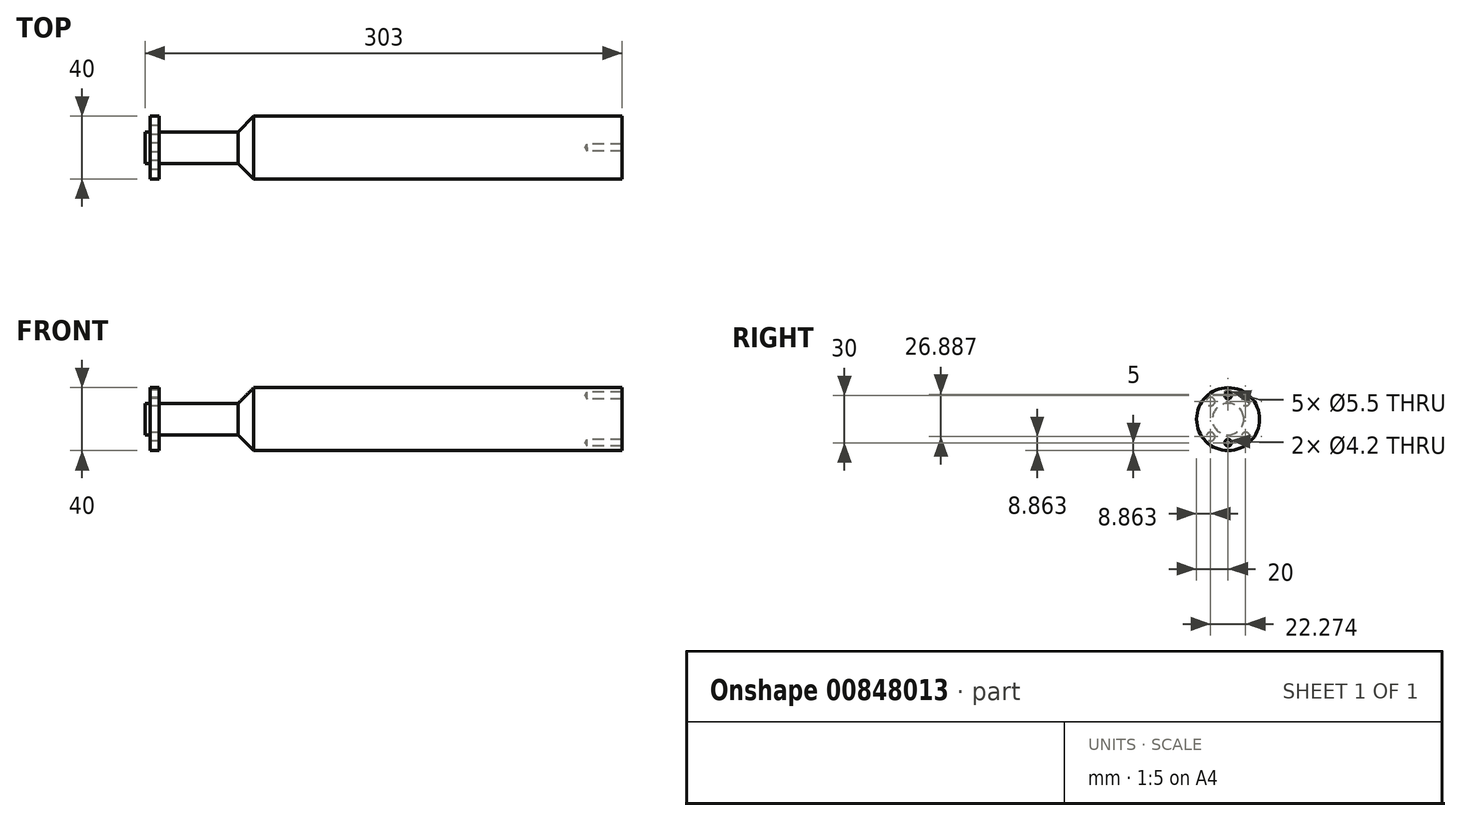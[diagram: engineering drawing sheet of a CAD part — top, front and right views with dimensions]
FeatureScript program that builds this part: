
annotation { "Feature Type Name" : "Feature", "Feature Type Description" : "" }
export const myFeature = defineFeature(function(context is Context, id is Id, definition is map)
    precondition{}
    {
        {
            var Q0;
            Q0=qCreatedBy(makeId("Front.planeOp"),FACE);
            var sketch = newSketch(context, id + "F0", { "sketchPlane" : qUnion([Q0])});
            skLineSegment(sketch, "E0", {"start": v(-163.2, 0) * mm, "end": v(136.8, 0) * mm});
            skLineSegment(sketch, "E1", {"start": v(136.8, 0) * mm, "end": v(136.8, 20) * mm});
            skLineSegment(sketch, "E2", {"start": v(136.8, 20) * mm, "end": v(-97.2, 20) * mm});
            skLineSegment(sketch, "E3", {"start": v(-97.2, 20) * mm, "end": v(-107.2, 10) * mm});
            skLineSegment(sketch, "E4", {"start": v(-107.2, 10) * mm, "end": v(-156.7, 10) * mm});
            skLineSegment(sketch, "E5", {"start": v(-157.2, 10.5) * mm, "end": v(-157.2, 20) * mm});
            skLineSegment(sketch, "E6", {"start": v(-163.2, 20) * mm, "end": v(-163.2, 10.5) * mm});
            skLineSegment(sketch, "E7", {"start": v(-163.7, 10) * mm, "end": v(-166.2, 10) * mm});
            skLineSegment(sketch, "E8", {"start": v(-166.2, 10) * mm, "end": v(-166.2, 0) * mm});
            skLineSegment(sketch, "E9", {"start": v(-166.2, 0) * mm, "end": v(-163.2, 0) * mm});
            skLineSegment(sketch, "E10", {"start": v(-163.2, 20) * mm, "end": v(-157.2, 20) * mm});
            skPoint(sketch, "E11.visualSharp", {"position": v(-157.2, 10) * mm});
            skArc(sketch, "E11.filletArc", {"start": v(-157.2, 10.5) * mm, "mid": v(-157.05, 10.15) * mm, "end": v(-156.7, 10) * mm});
            skPoint(sketch, "E12.visualSharp", {"position": v(-163.2, 10) * mm});
            skArc(sketch, "E12.filletArc", {"start": v(-163.7, 10) * mm, "mid": v(-163.34, 10.15) * mm, "end": v(-163.2, 10.5) * mm});
            skLineSegment(sketch, "E13", {"start": v(-204.84, 0) * mm, "end": v(203.32, 0) * mm, "construction": true});
            skSolve(sketch);
        }
        {
            var Q0;
            Q0=makeQuery(id+"F0.imprint","IMPRINT",FACE,{"disambiguationData":[TD([[makeQuery(id+"F0.imprint","IMPRINT",EDGE,{"derivedFrom":sQuery(id+"F0.wireOp",EDGE,"E0")}),1.0]])]});
            var Q1;
            Q1 = qConstructionFilter(qBodyType(qCreatedBy(id + "F0" ,EDGE), BodyType.WIRE), ConstructionObject.NO);
            var Q2;
            Q2=sQuery(id+"F0.wireOp",EDGE,"E13");
            revolve(context, id + "F1", {"surfaceOperationType" : NewSurfaceOperationType.NEW, "entities" : qUnion([Q0]), "surfaceEntities" : qUnion([Q1]), "axis" : qUnion([Q2]), "revolveType" : RevolveType.FULL});
        }
        {
            var Q0;
            Q0=makeQuery(id+"F1.opRevolve","SWEPT_FACE",FACE,{"disambiguationData":[OSD([sQuery(id+"F0.wireOp",EDGE,"E6")])]});
            var sketch = newSketch(context, id + "F2", { "sketchPlane" : qUnion([Q0])});
            skLineSegment(sketch, "E14", {"start": v(0, 0) * mm, "end": v(0, 29.49) * mm, "construction": true});
            skCircle(sketch, "E15", {"center": v(0, 0) * mm, "radius": 15.75 * mm, "construction": true});
            skCircle(sketch, "E16", {"center": v(0, 15.75) * mm, "radius": 2.75 * mm});
            skLineSegment(sketch, "E17", {"start": v(0, 0) * mm, "end": v(-11.14, 11.14) * mm, "construction": true});
            skCircle(sketch, "E18", {"center": v(-11.14, 11.14) * mm, "radius": 2.75 * mm});
            skCircle(sketch, "E19.1.0", {"center": v(-11.14, -11.14) * mm, "radius": 2.75 * mm});
            skCircle(sketch, "E19.2.0", {"center": v(11.14, -11.14) * mm, "radius": 2.75 * mm});
            skCircle(sketch, "E19.3.0", {"center": v(11.14, 11.14) * mm, "radius": 2.75 * mm});
            skLineSegment(sketch, "E20", {"start": v(0, 0) * mm, "end": v(-11.14, -11.14) * mm, "construction": true});
            skLineSegment(sketch, "E21", {"start": v(0, 0) * mm, "end": v(11.14, -11.14) * mm, "construction": true});
            skLineSegment(sketch, "E22", {"start": v(0, 0) * mm, "end": v(11.14, 11.14) * mm, "construction": true});
            skSolve(sketch);
        }
        {
            var Q0;
            Q0 = qSketchRegion(id + "F2", true);
            extrude(context, id + "F3", {"entities" : qUnion([Q0]), "operationType" : NewBodyOperationType.REMOVE, "oppositeDirection" : true, "depth" : 25 * mm, "offsetDistance" : 25 * mm});
        }
        {
            var Q0;
            Q0=makeQuery(id+"F1.opRevolve","SWEPT_FACE",FACE,{"disambiguationData":[OSD([sQuery(id+"F0.wireOp",EDGE,"E1")])]});
            var sketch = newSketch(context, id + "F4", { "sketchPlane" : qUnion([Q0])});
            skLineSegment(sketch, "E23", {"start": v(0, -20) * mm, "end": v(0, 20) * mm, "construction": true});
            skLineSegment(sketch, "E24", {"start": v(-20, 0) * mm, "end": v(20, 0) * mm, "construction": true});
            skCircle(sketch, "E25", {"center": v(0, 0) * mm, "radius": 15 * mm, "construction": true});
            skPoint(sketch, "E26", {"position": v(0, 15) * mm});
            skPoint(sketch, "E27", {"position": v(0, -15) * mm});
            skSolve(sketch);
        }
        {
            var Q0;
            Q0=sQuery(id+"F4.wireOp",VERTEX,"E26");
            var Q1;
            Q1=sQuery(id+"F4.wireOp",VERTEX,"E27");
            var Q2;
            Q2=makeQuery(id+"F1.opRevolve","SWEPT_BODY",BODY,{"disambiguationData":[OSD([sQuery(id+"F0.wireOp",EDGE,"E0"),sQuery(id+"F0.wireOp",EDGE,"E1"),sQuery(id+"F0.wireOp",EDGE,"E2"),sQuery(id+"F0.wireOp",EDGE,"E3"),sQuery(id+"F0.wireOp",EDGE,"E4"),sQuery(id+"F0.wireOp",EDGE,"E5"),sQuery(id+"F0.wireOp",EDGE,"E6"),sQuery(id+"F0.wireOp",EDGE,"E7"),sQuery(id+"F0.wireOp",EDGE,"E8"),sQuery(id+"F0.wireOp",EDGE,"E9"),sQuery(id+"F0.wireOp",EDGE,"E10"),sQuery(id+"F0.wireOp",EDGE,"E11.filletArc"),sQuery(id+"F0.wireOp",EDGE,"E12.filletArc")])]});
            hole(context, id + "F5", {"style" : HoleStyle.SIMPLE, "endStyle" : HoleEndStyle.BLIND, "standardTappedOrClearance" : lookupTablePath({ "standard" : "ISO", "engagement" : "75%", "pitch" : "0.8 mm", "size" : "M5", "type" : "Tapped" }), "standardBlindInLast" : lookupTablePath({ "standard" : "ISO", "engagement" : "75%", "pitch" : "0.8 mm", "size" : "M5", "type" : "Tapped" }), "holeDiameter" : 4.2 * mm, "majorDiameter" : 5 * mm, "showTappedDepth" : true, "holeDepth" : 22.4 * mm, "tappedDepth" : 20 * mm, "tapClearance" : 3, "locations" : qUnion([Q0, Q1]), "scope" : qUnion([Q2])});
        }
    });
